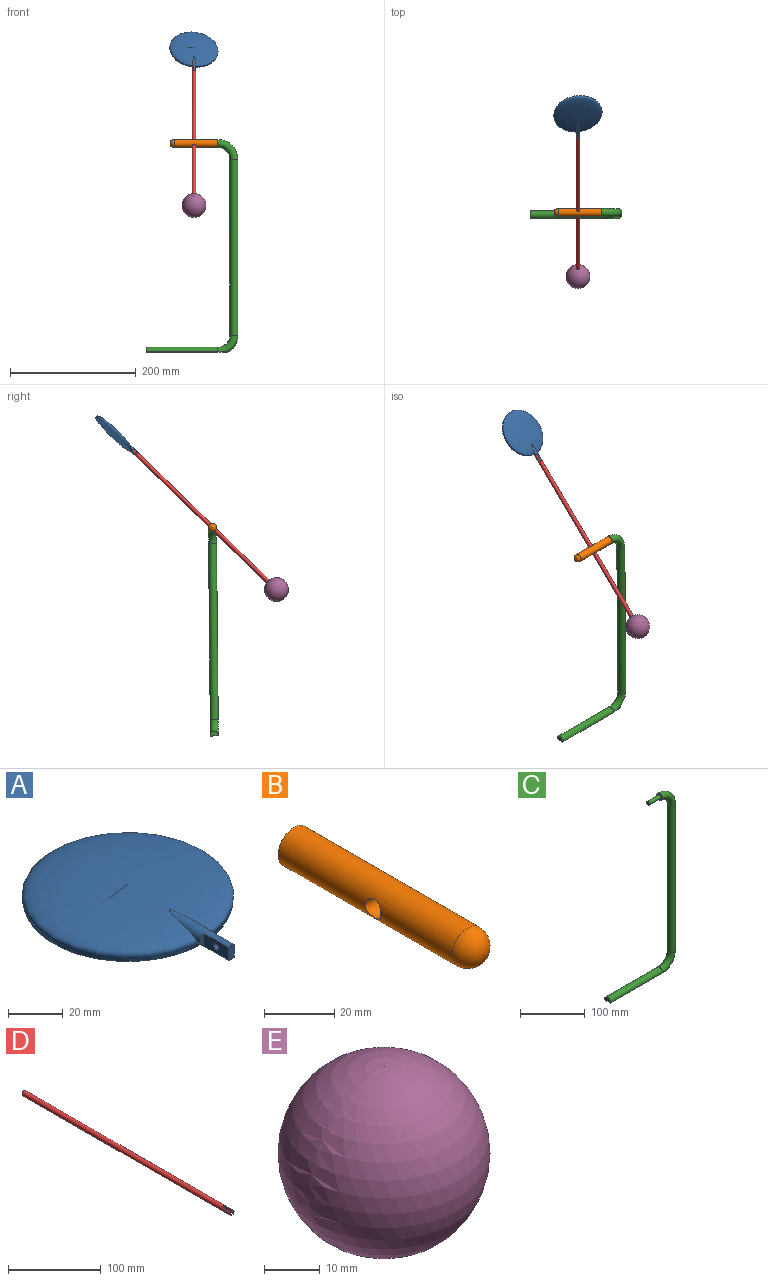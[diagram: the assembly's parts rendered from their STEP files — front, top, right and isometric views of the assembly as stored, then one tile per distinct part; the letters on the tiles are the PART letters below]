
ASSEMBLY  parts=5 mates=4
PART A: 9 faces, bbox 77.4x92.1x7.6 mm
  f0: plane 6.35x2.87mm, normal (0,-1,0), area 17.6mm2, adj f3,f4,f6
  f1: revolved ~77.44x77.44mm, area 5561.7mm2, adj f2,f3
  f2: plane 76.2x76.2mm, normal (0,0,-1), area 4560.4mm2, adj f1
  f3: cylinder r=3.17mm len=31.87mm, axis (0,1,0), area 203.9mm2, adj f0,f1,f4,f5,f6,f7
  f4: plane 12.7x5.66mm, normal (-1,0,0), area 66.9mm2, adj f0,f3,f5,f8
  f5: plane 5.66x1.74mm, normal (0,-1,0), area 7mm2, adj f3,f4
  f6: plane 12.7x5.66mm, normal (1,0,0), area 66.9mm2, adj f0,f3,f7,f8
  f7: plane 5.66x1.74mm, normal (0,-1,0), area 7mm2, adj f3,f6
  f8: cylinder r=1.27mm len=2.87mm, axis (1,0,0), area 22.9mm2, adj f4,f6
PART B: 6 faces, bbox 12.7x76.2x12.7 mm
  f0: cylinder r=6.35mm len=69.85mm, axis (0,1,0), area 2721.5mm2, adj f1,f2,f3
  f1: plane 12.7x12.7mm, normal (0,1,0), area 95mm2, adj f0,f4
  f2: cylinder r=3.17mm len=12.7mm, axis (1,0,0), area 236.7mm2, adj f0
  f3: sphere r=6.35mm, area 253.4mm2, adj f0
  f4: cylinder r=3.17mm len=25.4mm, axis (0,1,0), area 506.7mm2, adj f1,f5
  f5: plane 6.35x6.35mm, normal (0,1,0), area 31.7mm2, adj f4
PART C: 9 faces, bbox 148.7x12.7x348.1 mm
  f0: cylinder r=6.35mm len=114.3mm, axis (-1,0,0), area 2572.5mm2, adj f1,f2,f6
  f1: plane 12.7x7.62mm, normal (-1,0,0), area 79.4mm2, adj f0,f6
  f2: torus R=25.4mm, axis (0,1,0), area 1354.6mm2, adj f0,f5,f6
  f3: plane 12.7x12.7mm, normal (-1,0,0), area 95mm2, adj f4,f7
  f4: torus R=25.4mm, axis (0,1,0), area 1591.9mm2, adj f3,f5
  f5: cylinder r=6.35mm len=279.4mm, axis (0,0,-1), area 11147.6mm2, adj f2,f4
  f6: plane 131.53x12.45mm, normal (0,0,-1), area 1602.1mm2, adj f0,f1,f2
  f7: cylinder r=3.17mm len=25.4mm, axis (1,0,0), area 506.7mm2, adj f3,f8
  f8: plane 6.35x6.35mm, normal (-1,0,0), area 31.7mm2, adj f7
PART D: 9 faces, bbox 6.4x317.5x6.4 mm
  f0: cylinder r=3.17mm len=317.5mm, axis (0,1,0), area 6248.2mm2, adj f1,f2,f3,f4,f5,f6,f7,f8
  f1: plane 5.63x2.1mm, normal (0,-1,0), area 7.1mm2, adj f0,f4
  f2: plane 5.63x2.1mm, normal (0,-1,0), area 7.1mm2, adj f0,f5
  f3: plane 6.35x6.35mm, normal (0,1,0), area 31.7mm2, adj f0
  f4: plane 12.7x5.63mm, normal (-0.99,0,-0.12), area 66.9mm2, adj f0,f1,f6,f8
  f5: plane 12.7x5.63mm, normal (0.99,0,0.12), area 66.9mm2, adj f0,f2,f6,f7
  f6: plane 6.35x3.51mm, normal (0,-1,0), area 17.5mm2, adj f0,f4,f5
  f7: cylinder r=1.27mm len=2.54mm, axis (1,0,0), area 12.8mm2, adj f0,f5
  f8: cylinder r=1.27mm len=2.54mm, axis (-1,0,0), area 12.8mm2, adj f0,f4
PART E: 3 faces, bbox 38.1x38.1x38.1 mm
  f0: sphere r=19.05mm, area 4528.5mm2, adj f1
  f1: cylinder r=3.17mm len=18.78mm, axis (0,-1,0), area 374.7mm2, adj f0,f2
  f2: plane 6.35x6.35mm, normal (0,1,0), area 31.7mm2, adj f1
PLACE A rot(axis=(0.99,0.15,0.06),44.6deg) t=(-60.8,83.15,444.11)mm
PLACE B rot(axis=(0.35,0.35,-0.87),98.1deg) t=(-22.24,-74.92,296.23)mm
PLACE C rot(axis=(-1,0,0),0.5deg) t=(3.16,-77.82,-8.56)mm
PLACE D rot(axis=(-1,0,0),135.9deg) t=(-60.34,-176.7,197.62)mm
PLACE E rot(axis=(1,0,0),44.1deg) t=(-60.34,-176.7,197.62)mm
MATE revolute C.f7 <-> B.f4  axis (-1,0,0) through (-47.64,-74.92,296.23)mm
MATE fastened D.f4 <-> A.f6  axis (-0.99,-0.08,0.09) through (-58.92,51.45,418.43)mm
MATE slider D.f0 <-> B.f2  axis (0,-0.72,-0.7) through (-60.34,-62.68,308.09)mm
MATE fastened E.f1 <-> D.f0  axis (0,0.72,0.7) through (-60.34,-176.7,197.62)mm
